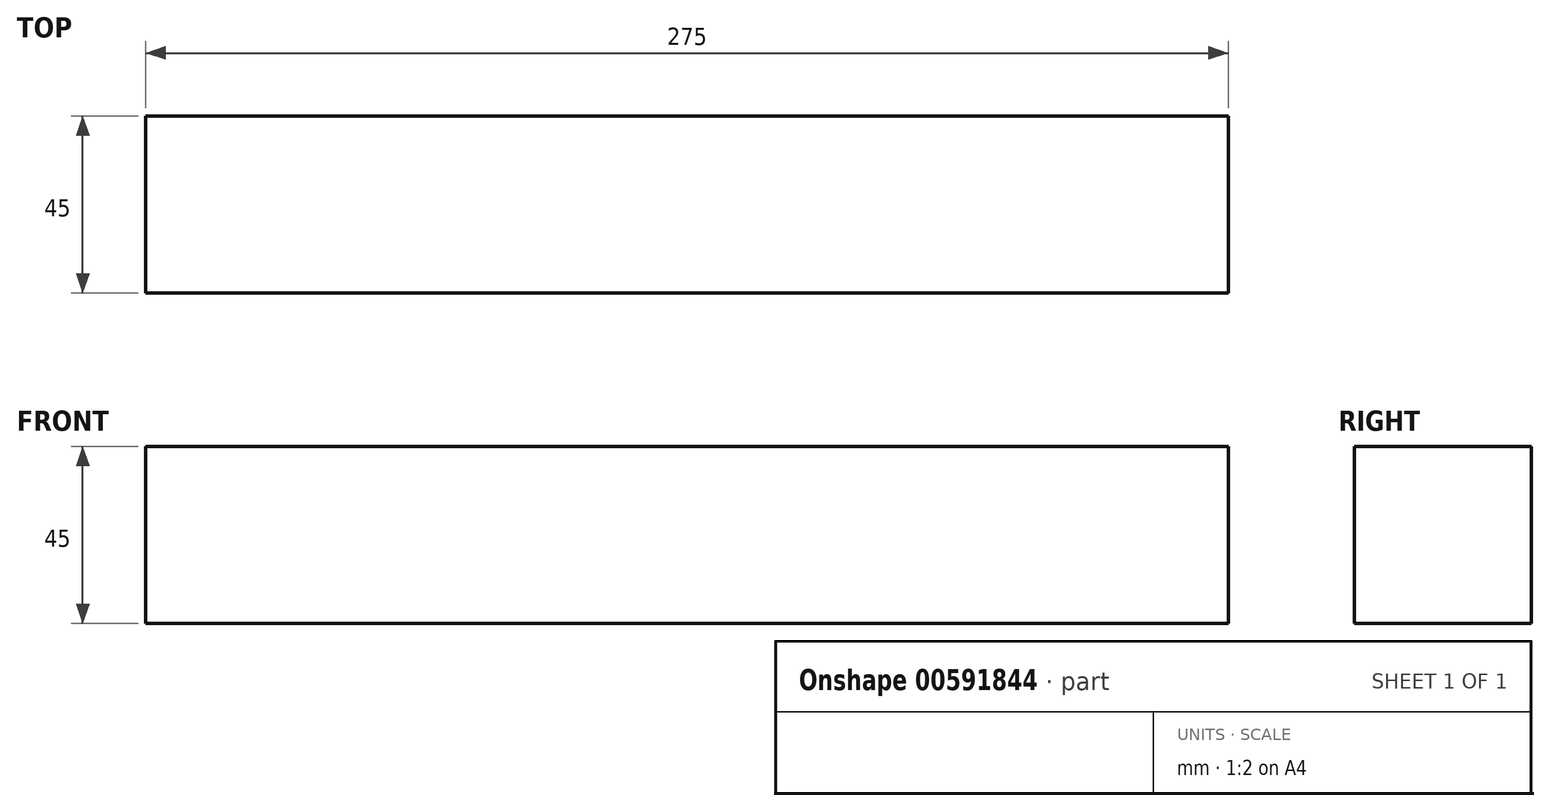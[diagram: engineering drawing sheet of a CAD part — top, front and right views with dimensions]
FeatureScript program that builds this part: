
annotation { "Feature Type Name" : "Feature", "Feature Type Description" : "" }
export const myFeature = defineFeature(function(context is Context, id is Id, definition is map)
    precondition{}
    {
        {
            var Q0;
            Q0=qCreatedBy(makeId("Right.planeOp"),FACE);
            var sketch = newSketch(context, id + "F0", { "sketchPlane" : qUnion([Q0])});
            skLineSegment(sketch, "E0.bottom", {"start": v(0, 0) * mm, "end": v(45, 0) * mm});
            skLineSegment(sketch, "E0.top", {"start": v(0, 45) * mm, "end": v(45, 45) * mm});
            skLineSegment(sketch, "E0.left", {"start": v(0, 0) * mm, "end": v(0, 45) * mm});
            skLineSegment(sketch, "E0.right", {"start": v(45, 0) * mm, "end": v(45, 45) * mm});
            skSolve(sketch);
        }
        {
            var Q0;
            Q0=makeQuery(id+"F0.imprint","IMPRINT",FACE,{"disambiguationData":[TD([[makeQuery(id+"F0.imprint","IMPRINT",EDGE,{"derivedFrom":sQuery(id+"F0.wireOp",EDGE,"E0.bottom")}),1.0]])]});
            extrude(context, id + "F1", {"entities" : qUnion([Q0]), "depth" : 275 * mm, "offsetDistance" : 25 * mm});
        }
    });
